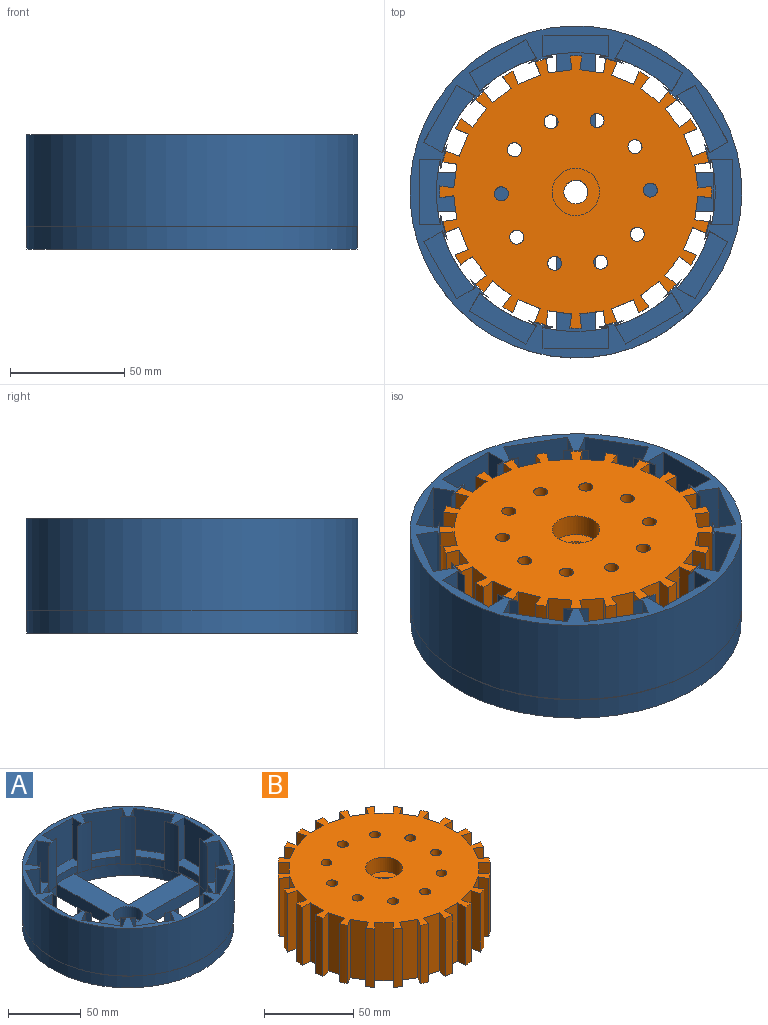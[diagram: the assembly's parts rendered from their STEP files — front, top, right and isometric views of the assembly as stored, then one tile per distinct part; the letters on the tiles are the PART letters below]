
ASSEMBLY  parts=2 mates=1
PART A: 137 faces, bbox 145.5x145.5x50 mm
  f0: cylinder r=5.26mm len=10.52mm, axis (0,0,1), area 33mm2, adj f23,f135
  f1: plane 24.96x14.43mm, normal (0,0,1), area 1.2mm2, adj f13,f103,f105,f112
  f2: plane 24.96x14.43mm, normal (0,0,1), area 1.2mm2, adj f13,f97,f99,f114
  f3: plane 122.33x122.33mm, normal (0,0,1), area 3574mm2, adj f10,f11,f12,f13,f14,f15,f16,f17
  f4: plane 24.96x14.43mm, normal (0,0,1), area 1.2mm2, adj f14,f85,f87,f118
  f5: plane 24.96x14.43mm, normal (0,0,1), area 1.2mm2, adj f14,f79,f81,f120
  f6: plane 24.96x14.43mm, normal (0,0,1), area 1.2mm2, adj f16,f67,f69,f124
  f7: plane 24.96x14.43mm, normal (0,0,1), area 1.2mm2, adj f16,f61,f63,f126
  f8: plane 24.96x14.43mm, normal (0,0,1), area 1.2mm2, adj f11,f49,f51,f130
  f9: plane 24.96x14.43mm, normal (0,0,1), area 1.2mm2, adj f11,f43,f45,f132
  f10: plane 51.98x10mm, normal (1,0,0), area 519.8mm2, adj f3,f11,f19,f23
  f11: cylinder r=61.12mm len=51.98mm, axis (0,0,1), area 788.1mm2, adj f3,f8,f9,f10,f19,f23,f33,f34
  f12: plane 51.9x10mm, normal (0,1,0), area 519mm2, adj f3,f13,f20,f23
  f13: cylinder r=61.12mm len=51.98mm, axis (0,0,1), area 788.1mm2, adj f1,f2,f3,f12,f20,f23,f30,f31
  f14: cylinder r=61.12mm len=51.98mm, axis (0,0,1), area 788.1mm2, adj f3,f4,f5,f15,f21,f23,f27,f28
  f15: plane 51.9x10mm, normal (0,-1,0), area 519mm2, adj f3,f14,f21,f23
  f16: cylinder r=61.12mm len=51.98mm, axis (0,0,1), area 788.1mm2, adj f3,f6,f7,f17,f22,f23,f24,f25
  f17: plane 51.98x10mm, normal (1,0,0), area 519.8mm2, adj f3,f16,f22,f23
  f18: cylinder r=72.41mm len=144.82mm, axis (0,0,1), area 4549.7mm2, adj f23,f110
  f19: plane 51.9x10mm, normal (0,1,0), area 519mm2, adj f3,f10,f11,f23
  f20: plane 51.98x10mm, normal (-1,0,0), area 519.8mm2, adj f3,f12,f13,f23
  f21: plane 51.98x10mm, normal (-1,0,0), area 519.8mm2, adj f3,f14,f15,f23
  f22: plane 51.9x10mm, normal (0,-1,0), area 519mm2, adj f3,f16,f17,f23
  f23: plane 144.82x144.82mm, normal (0,0,-1), area 8533.6mm2, adj f0,f10,f11,f12,f13,f14,f15,f16
  f24: plane 10.46x3.03mm, normal (0,0,-1), area 6.2mm2, adj f16,f69,f70,f71,f72,f73
  f25: plane 7.66x7.66mm, normal (0,0,-1), area 6.2mm2, adj f16,f63,f64,f65,f66,f67
  f26: plane 10.46x3.03mm, normal (0,0,-1), area 6.2mm2, adj f16,f57,f58,f59,f60,f61
  f27: plane 10.46x3.03mm, normal (0,0,-1), area 6.2mm2, adj f14,f87,f88,f89,f90,f91
  f28: plane 7.66x7.66mm, normal (0,0,-1), area 6.2mm2, adj f14,f81,f82,f83,f84,f85
  f29: plane 10.46x3.03mm, normal (0,0,-1), area 6.2mm2, adj f14,f75,f76,f77,f78,f79
  f30: plane 10.46x3.03mm, normal (0,0,-1), area 6.2mm2, adj f13,f36,f37,f105,f106,f107
  f31: plane 7.66x7.66mm, normal (0,0,-1), area 6.2mm2, adj f13,f99,f100,f101,f102,f103
  f32: plane 10.46x3.03mm, normal (0,0,-1), area 6.2mm2, adj f13,f93,f94,f95,f96,f97
  f33: plane 10.46x3.03mm, normal (0,0,-1), area 6.2mm2, adj f11,f51,f52,f53,f54,f55
  f34: plane 7.66x7.66mm, normal (0,0,-1), area 6.2mm2, adj f11,f45,f46,f47,f48,f49
  f35: plane 10.46x3.03mm, normal (0,0,-1), area 6.2mm2, adj f11,f39,f40,f41,f42,f43
  f36: plane 40x4.14mm, normal (0,1,0), area 165.7mm2, adj f30,f37,f107,f109
  f37: plane 40x9.51mm, normal (1,0,0), area 325mm2, adj f3,f30,f36,f38,f109,f133,f134
  f38: plane 34x28.79mm, normal (0,-1,0), area 978.9mm2, adj f37,f39,f109,f133
  f39: plane 40x9.51mm, normal (-1,0,0), area 325mm2, adj f3,f35,f38,f40,f109,f133,f134
  f40: plane 40x4.14mm, normal (0,1,0), area 165.7mm2, adj f35,f39,f41,f109
  f41: cylinder r=60.06mm len=40mm, axis (0,0,-1), area 433.6mm2, adj f35,f40,f42,f109
  f42: plane 40x3.59mm, normal (0.5,0.87,0), area 165.7mm2, adj f35,f41,f43,f109
  f43: plane 40x8.24mm, normal (0.87,-0.5,0), area 325mm2, adj f9,f35,f42,f44,f109,f131,f132
  f44: plane 34x24.94mm, normal (-0.5,-0.87,0), area 978.9mm2, adj f43,f45,f109,f131
  f45: plane 40x8.24mm, normal (-0.87,0.5,0), area 325mm2, adj f9,f34,f44,f46,f109,f131,f132
  f46: plane 40x3.59mm, normal (0.5,0.87,0), area 165.7mm2, adj f34,f45,f47,f109
  f47: cylinder r=60.06mm len=40mm, axis (0,0,-1), area 433.6mm2, adj f34,f46,f48,f109
  f48: plane 40x3.59mm, normal (0.87,0.5,0), area 165.7mm2, adj f34,f47,f49,f109
  f49: plane 40x8.24mm, normal (0.5,-0.87,0), area 325mm2, adj f8,f34,f48,f50,f109,f129,f130
  f50: plane 34x24.94mm, normal (-0.87,-0.5,0), area 978.9mm2, adj f49,f51,f109,f129
  f51: plane 40x8.24mm, normal (-0.5,0.87,0), area 325mm2, adj f8,f33,f50,f52,f109,f129,f130
  f52: plane 40x3.59mm, normal (0.87,0.5,0), area 165.7mm2, adj f33,f51,f53,f109
  f53: cylinder r=60.06mm len=40mm, axis (0,0,-1), area 433.6mm2, adj f33,f52,f54,f109
  f54: plane 40x4.14mm, normal (1,0,0), area 165.7mm2, adj f33,f53,f55,f109
  f55: plane 40x9.51mm, normal (0,-1,0), area 325mm2, adj f3,f33,f54,f56,f109,f127,f128
  f56: plane 34x28.79mm, normal (-1,0,0), area 978.9mm2, adj f55,f57,f109,f127
  f57: plane 40x9.51mm, normal (0,1,0), area 325mm2, adj f3,f26,f56,f58,f109,f127,f128
  f58: plane 40x4.14mm, normal (1,0,0), area 165.7mm2, adj f26,f57,f59,f109
  f59: cylinder r=60.06mm len=40mm, axis (0,0,-1), area 433.6mm2, adj f26,f58,f60,f109
  f60: plane 40x3.59mm, normal (0.87,-0.5,0), area 165.7mm2, adj f26,f59,f61,f109
  f61: plane 40x8.24mm, normal (-0.5,-0.87,0), area 325mm2, adj f7,f26,f60,f62,f109,f125,f126
  f62: plane 34x24.94mm, normal (-0.87,0.5,0), area 978.9mm2, adj f61,f63,f109,f125
  f63: plane 40x8.24mm, normal (0.5,0.87,0), area 325mm2, adj f7,f25,f62,f64,f109,f125,f126
  f64: plane 40x3.59mm, normal (0.87,-0.5,0), area 165.7mm2, adj f25,f63,f65,f109
  f65: cylinder r=60.06mm len=40mm, axis (0,0,-1), area 433.6mm2, adj f25,f64,f66,f109
  f66: plane 40x3.59mm, normal (0.5,-0.87,0), area 165.7mm2, adj f25,f65,f67,f109
  f67: plane 40x8.24mm, normal (-0.87,-0.5,0), area 325mm2, adj f6,f25,f66,f68,f109,f123,f124
  f68: plane 34x24.94mm, normal (-0.5,0.87,0), area 978.9mm2, adj f67,f69,f109,f123
  f69: plane 40x8.24mm, normal (0.87,0.5,0), area 325mm2, adj f6,f24,f68,f70,f109,f123,f124
  f70: plane 40x3.59mm, normal (0.5,-0.87,0), area 165.7mm2, adj f24,f69,f71,f109
  f71: cylinder r=60.06mm len=40mm, axis (0,0,-1), area 433.6mm2, adj f24,f70,f72,f109
  f72: plane 40x4.14mm, normal (0,-1,0), area 165.7mm2, adj f24,f71,f73,f109
  f73: plane 40x9.51mm, normal (-1,0,0), area 325mm2, adj f3,f24,f72,f74,f109,f121,f122
  f74: plane 34x28.79mm, normal (0,1,0), area 978.9mm2, adj f73,f75,f109,f121
  f75: plane 40x9.51mm, normal (1,0,0), area 325mm2, adj f3,f29,f74,f76,f109,f121,f122
  f76: plane 40x4.14mm, normal (0,-1,0), area 165.7mm2, adj f29,f75,f77,f109
  f77: cylinder r=60.06mm len=40mm, axis (0,0,-1), area 433.6mm2, adj f29,f76,f78,f109
  f78: plane 40x3.59mm, normal (-0.5,-0.87,0), area 165.7mm2, adj f29,f77,f79,f109
  f79: plane 40x8.24mm, normal (-0.87,0.5,0), area 325mm2, adj f5,f29,f78,f80,f109,f119,f120
  f80: plane 34x24.94mm, normal (0.5,0.87,0), area 978.9mm2, adj f79,f81,f109,f119
  f81: plane 40x8.24mm, normal (0.87,-0.5,0), area 325mm2, adj f5,f28,f80,f82,f109,f119,f120
  f82: plane 40x3.59mm, normal (-0.5,-0.87,0), area 165.7mm2, adj f28,f81,f83,f109
  f83: cylinder r=60.06mm len=40mm, axis (0,0,-1), area 433.6mm2, adj f28,f82,f84,f109
  f84: plane 40x3.59mm, normal (-0.87,-0.5,0), area 165.7mm2, adj f28,f83,f85,f109
  f85: plane 40x8.24mm, normal (-0.5,0.87,0), area 325mm2, adj f4,f28,f84,f86,f109,f117,f118
  f86: plane 34x24.94mm, normal (0.87,0.5,0), area 978.9mm2, adj f85,f87,f109,f117
  f87: plane 40x8.24mm, normal (0.5,-0.87,0), area 325mm2, adj f4,f27,f86,f88,f109,f117,f118
  f88: plane 40x3.59mm, normal (-0.87,-0.5,0), area 165.7mm2, adj f27,f87,f89,f109
  f89: cylinder r=60.06mm len=40mm, axis (0,0,-1), area 433.6mm2, adj f27,f88,f90,f109
  f90: plane 40x4.14mm, normal (-1,0,0), area 165.7mm2, adj f27,f89,f91,f109
  f91: plane 40x9.51mm, normal (0,1,0), area 325mm2, adj f3,f27,f90,f92,f109,f115,f116
  f92: plane 34x28.79mm, normal (1,0,0), area 978.9mm2, adj f91,f93,f109,f115
  f93: plane 40x9.51mm, normal (0,-1,0), area 325mm2, adj f3,f32,f92,f94,f109,f115,f116
  f94: plane 40x4.14mm, normal (-1,0,0), area 165.7mm2, adj f32,f93,f95,f109
  f95: cylinder r=60.06mm len=40mm, axis (0,0,-1), area 433.6mm2, adj f32,f94,f96,f109
  f96: plane 40x3.59mm, normal (-0.87,0.5,0), area 165.7mm2, adj f32,f95,f97,f109
  f97: plane 40x8.24mm, normal (0.5,0.87,0), area 325mm2, adj f2,f32,f96,f98,f109,f113,f114
  f98: plane 34x24.94mm, normal (0.87,-0.5,0), area 978.9mm2, adj f97,f99,f109,f113
  f99: plane 40x8.24mm, normal (-0.5,-0.87,0), area 325mm2, adj f2,f31,f98,f100,f109,f113,f114
  f100: plane 40x3.59mm, normal (-0.87,0.5,0), area 165.7mm2, adj f31,f99,f101,f109
  f101: cylinder r=60.06mm len=40mm, axis (0,0,-1), area 433.6mm2, adj f31,f100,f102,f109
  f102: plane 40x3.59mm, normal (-0.5,0.87,0), area 165.7mm2, adj f31,f101,f103,f109
  f103: plane 40x8.24mm, normal (0.87,0.5,0), area 325mm2, adj f1,f31,f102,f104,f109,f111,f112
  f104: plane 34x24.94mm, normal (0.5,-0.87,0), area 978.9mm2, adj f103,f105,f109,f111
  f105: plane 40x8.24mm, normal (-0.87,-0.5,0), area 325mm2, adj f1,f30,f104,f106,f109,f111,f112
  f106: plane 40x3.59mm, normal (-0.5,0.87,0), area 165.7mm2, adj f30,f105,f107,f109
  f107: cylinder r=60.06mm len=40mm, axis (0,0,-1), area 433.6mm2, adj f30,f36,f106,f109
  f108: cylinder r=72.76mm len=145.53mm, axis (0,0,-1), area 18287.3mm2, adj f109,f110
  f109: plane 145.53x145.53mm, normal (0,0,1), area 2158.4mm2, adj f36,f37,f38,f39,f40,f41,f42,f43
  f110: plane 145.53x145.53mm, normal (0,0,-1), area 160.2mm2, adj f18,f108
  f111: plane 29.56x22.4mm, normal (0,0,1), area 233mm2, adj f103,f104,f105,f112
  f112: cylinder r=61.17mm len=24.94mm, axis (0,0,-1), area 174.4mm2, adj f1,f103,f105,f111
  f113: plane 29.56x22.4mm, normal (0,0,1), area 233mm2, adj f97,f98,f99,f114
  f114: cylinder r=61.17mm len=24.94mm, axis (0,0,-1), area 174.4mm2, adj f2,f97,f99,f113
  f115: plane 28.79x9.24mm, normal (0,0,1), area 233mm2, adj f91,f92,f93,f116
  f116: cylinder r=61.17mm len=28.79mm, axis (0,0,-1), area 174.4mm2, adj f3,f91,f93,f115
  f117: plane 29.56x22.4mm, normal (0,0,1), area 233mm2, adj f85,f86,f87,f118
  f118: cylinder r=61.17mm len=24.94mm, axis (0,0,-1), area 174.4mm2, adj f4,f85,f87,f117
  f119: plane 29.56x22.4mm, normal (0,0,1), area 233mm2, adj f79,f80,f81,f120
  f120: cylinder r=61.17mm len=24.94mm, axis (0,0,-1), area 174.4mm2, adj f5,f79,f81,f119
  f121: plane 28.79x9.24mm, normal (0,0,1), area 233mm2, adj f73,f74,f75,f122
  f122: cylinder r=61.17mm len=28.79mm, axis (0,0,-1), area 174.4mm2, adj f3,f73,f75,f121
  f123: plane 29.56x22.4mm, normal (0,0,1), area 233mm2, adj f67,f68,f69,f124
  f124: cylinder r=61.17mm len=24.94mm, axis (0,0,-1), area 174.4mm2, adj f6,f67,f69,f123
  f125: plane 29.56x22.4mm, normal (0,0,1), area 233mm2, adj f61,f62,f63,f126
  f126: cylinder r=61.17mm len=24.94mm, axis (0,0,-1), area 174.4mm2, adj f7,f61,f63,f125
  f127: plane 28.79x9.24mm, normal (0,0,1), area 233mm2, adj f55,f56,f57,f128
  f128: cylinder r=61.17mm len=28.79mm, axis (0,0,-1), area 174.4mm2, adj f3,f55,f57,f127
  f129: plane 29.56x22.4mm, normal (0,0,1), area 233mm2, adj f49,f50,f51,f130
  f130: cylinder r=61.17mm len=24.94mm, axis (0,0,-1), area 174.4mm2, adj f8,f49,f51,f129
  f131: plane 29.56x22.4mm, normal (0,0,1), area 233mm2, adj f43,f44,f45,f132
  f132: cylinder r=61.17mm len=24.94mm, axis (0,0,-1), area 174.4mm2, adj f9,f43,f45,f131
  f133: plane 28.79x9.24mm, normal (0,0,1), area 233mm2, adj f37,f38,f39,f134
  f134: cylinder r=61.17mm len=28.79mm, axis (0,0,-1), area 174.4mm2, adj f3,f37,f39,f133
  f135: plane 20.08x20.08mm, normal (0,0,1), area 229.7mm2, adj f0,f136
  f136: cylinder r=10.04mm len=20.08mm, axis (0,0,1), area 567.6mm2, adj f3,f135
PART B: 111 faces, bbox 118.9x118.9x40 mm
  f0: cylinder r=5.24mm len=30mm, axis (0,0,-1), area 987.7mm2, adj f98,f100
  f1: plane 40x6.18mm, normal (1,0,0), area 247mm2, adj f2,f96,f97,f98
  f2: cylinder r=59.69mm len=40mm, axis (0,0,-1), area 205.3mm2, adj f1,f3,f97,f98
  f3: plane 40x5.97mm, normal (-0.97,-0.26,0), area 247mm2, adj f2,f4,f97,f98
  f4: plane 40x10.12mm, normal (-0.26,0.97,0), area 419.2mm2, adj f3,f5,f97,f98
  f5: plane 40x5.97mm, normal (0.97,0.26,0), area 247mm2, adj f4,f6,f97,f98
  f6: cylinder r=59.69mm len=40mm, axis (0,0,-1), area 205.3mm2, adj f5,f7,f97,f98
  f7: plane 40x5.35mm, normal (-0.87,-0.5,0), area 247mm2, adj f6,f8,f97,f98
  f8: plane 40x9.08mm, normal (-0.5,0.87,0), area 419.2mm2, adj f7,f9,f97,f98
  f9: plane 40x5.35mm, normal (0.87,0.5,0), area 247mm2, adj f8,f10,f97,f98
  f10: cylinder r=59.69mm len=40mm, axis (0,0,-1), area 205.3mm2, adj f9,f11,f97,f98
  f11: plane 40x4.37mm, normal (-0.71,-0.71,0), area 247mm2, adj f10,f12,f97,f98
  f12: plane 40x7.41mm, normal (-0.71,0.71,0), area 419.2mm2, adj f11,f13,f97,f98
  f13: plane 40x4.37mm, normal (0.71,0.71,0), area 247mm2, adj f12,f14,f97,f98
  f14: cylinder r=59.69mm len=40mm, axis (0,0,-1), area 205.3mm2, adj f13,f15,f97,f98
  f15: plane 40x5.35mm, normal (-0.5,-0.87,0), area 247mm2, adj f14,f16,f97,f98
  f16: plane 40x9.08mm, normal (-0.87,0.5,0), area 419.2mm2, adj f15,f17,f97,f98
  f17: plane 40x5.35mm, normal (0.5,0.87,0), area 247mm2, adj f16,f18,f97,f98
  f18: cylinder r=59.69mm len=40mm, axis (0,0,-1), area 205.3mm2, adj f17,f19,f97,f98
  f19: plane 40x5.97mm, normal (-0.26,-0.97,0), area 247mm2, adj f18,f20,f97,f98
  f20: plane 40x10.12mm, normal (-0.97,0.26,0), area 419.2mm2, adj f19,f21,f97,f98
  f21: plane 40x5.97mm, normal (0.26,0.97,0), area 247mm2, adj f20,f22,f97,f98
  f22: cylinder r=59.69mm len=40mm, axis (0,0,-1), area 205.3mm2, adj f21,f23,f97,f98
  f23: plane 40x6.18mm, normal (0,-1,0), area 247mm2, adj f22,f24,f97,f98
  f24: plane 40x10.48mm, normal (-1,0,0), area 419.2mm2, adj f23,f25,f97,f98
  f25: plane 40x6.18mm, normal (0,1,0), area 247mm2, adj f24,f26,f97,f98
  f26: cylinder r=59.69mm len=40mm, axis (0,0,-1), area 205.3mm2, adj f25,f27,f97,f98
  f27: plane 40x5.97mm, normal (0.26,-0.97,0), area 247mm2, adj f26,f28,f97,f98
  f28: plane 40x10.12mm, normal (-0.97,-0.26,0), area 419.2mm2, adj f27,f29,f97,f98
  f29: plane 40x5.97mm, normal (-0.26,0.97,0), area 247mm2, adj f28,f30,f97,f98
  f30: cylinder r=59.69mm len=40mm, axis (0,0,-1), area 205.3mm2, adj f29,f31,f97,f98
  f31: plane 40x5.35mm, normal (0.5,-0.87,0), area 247mm2, adj f30,f32,f97,f98
  f32: plane 40x9.08mm, normal (-0.87,-0.5,0), area 419.2mm2, adj f31,f33,f97,f98
  f33: plane 40x5.35mm, normal (-0.5,0.87,0), area 247mm2, adj f32,f34,f97,f98
  f34: cylinder r=59.69mm len=40mm, axis (0,0,-1), area 205.3mm2, adj f33,f35,f97,f98
  f35: plane 40x4.37mm, normal (0.71,-0.71,0), area 247mm2, adj f34,f36,f97,f98
  f36: plane 40x7.41mm, normal (-0.71,-0.71,0), area 419.2mm2, adj f35,f37,f97,f98
  f37: plane 40x4.37mm, normal (-0.71,0.71,0), area 247mm2, adj f36,f38,f97,f98
  f38: cylinder r=59.69mm len=40mm, axis (0,0,-1), area 205.3mm2, adj f37,f39,f97,f98
  f39: plane 40x5.35mm, normal (0.87,-0.5,0), area 247mm2, adj f38,f40,f97,f98
  f40: plane 40x9.08mm, normal (-0.5,-0.87,0), area 419.2mm2, adj f39,f41,f97,f98
  f41: plane 40x5.35mm, normal (-0.87,0.5,0), area 247mm2, adj f40,f42,f97,f98
  f42: cylinder r=59.69mm len=40mm, axis (0,0,-1), area 205.3mm2, adj f41,f43,f97,f98
  f43: plane 40x5.97mm, normal (0.97,-0.26,0), area 247mm2, adj f42,f44,f97,f98
  f44: plane 40x10.12mm, normal (-0.26,-0.97,0), area 419.2mm2, adj f43,f45,f97,f98
  f45: plane 40x5.97mm, normal (-0.97,0.26,0), area 247mm2, adj f44,f46,f97,f98
  f46: cylinder r=59.69mm len=40mm, axis (0,0,-1), area 205.3mm2, adj f45,f47,f97,f98
  f47: plane 40x6.18mm, normal (1,0,0), area 247mm2, adj f46,f48,f97,f98
  f48: plane 40x10.48mm, normal (0,-1,0), area 419.2mm2, adj f47,f49,f97,f98
  f49: plane 40x6.18mm, normal (-1,0,0), area 247mm2, adj f48,f50,f97,f98
  f50: cylinder r=59.69mm len=40mm, axis (0,0,-1), area 205.3mm2, adj f49,f51,f97,f98
  f51: plane 40x5.97mm, normal (0.97,0.26,0), area 247mm2, adj f50,f52,f97,f98
  f52: plane 40x10.12mm, normal (0.26,-0.97,0), area 419.2mm2, adj f51,f53,f97,f98
  f53: plane 40x5.97mm, normal (-0.97,-0.26,0), area 247mm2, adj f52,f54,f97,f98
  f54: cylinder r=59.69mm len=40mm, axis (0,0,-1), area 205.3mm2, adj f53,f55,f97,f98
  f55: plane 40x5.35mm, normal (0.87,0.5,0), area 247mm2, adj f54,f56,f97,f98
  f56: plane 40x9.08mm, normal (0.5,-0.87,0), area 419.2mm2, adj f55,f57,f97,f98
  f57: plane 40x5.35mm, normal (-0.87,-0.5,0), area 247mm2, adj f56,f58,f97,f98
  f58: cylinder r=59.69mm len=40mm, axis (0,0,-1), area 205.3mm2, adj f57,f59,f97,f98
  f59: plane 40x4.37mm, normal (0.71,0.71,0), area 247mm2, adj f58,f60,f97,f98
  f60: plane 40x7.41mm, normal (0.71,-0.71,0), area 419.2mm2, adj f59,f61,f97,f98
  f61: plane 40x4.37mm, normal (-0.71,-0.71,0), area 247mm2, adj f60,f62,f97,f98
  f62: cylinder r=59.69mm len=40mm, axis (0,0,-1), area 205.3mm2, adj f61,f63,f97,f98
  f63: plane 40x5.35mm, normal (0.5,0.87,0), area 247mm2, adj f62,f64,f97,f98
  f64: plane 40x9.08mm, normal (0.87,-0.5,0), area 419.2mm2, adj f63,f65,f97,f98
  f65: plane 40x5.35mm, normal (-0.5,-0.87,0), area 247mm2, adj f64,f66,f97,f98
  f66: cylinder r=59.69mm len=40mm, axis (0,0,-1), area 205.3mm2, adj f65,f67,f97,f98
  f67: plane 40x5.97mm, normal (0.26,0.97,0), area 247mm2, adj f66,f68,f97,f98
  f68: plane 40x10.12mm, normal (0.97,-0.26,0), area 419.2mm2, adj f67,f69,f97,f98
  f69: plane 40x5.97mm, normal (-0.26,-0.97,0), area 247mm2, adj f68,f70,f97,f98
  f70: cylinder r=59.69mm len=40mm, axis (0,0,-1), area 205.3mm2, adj f69,f71,f97,f98
  f71: plane 40x6.18mm, normal (0,1,0), area 247mm2, adj f70,f72,f97,f98
  f72: plane 40x10.48mm, normal (1,0,0), area 419.2mm2, adj f71,f73,f97,f98
  f73: plane 40x6.18mm, normal (0,-1,0), area 247mm2, adj f72,f74,f97,f98
  f74: cylinder r=59.69mm len=40mm, axis (0,0,-1), area 205.3mm2, adj f73,f75,f97,f98
  f75: plane 40x5.97mm, normal (-0.26,0.97,0), area 247mm2, adj f74,f76,f97,f98
  f76: plane 40x10.12mm, normal (0.97,0.26,0), area 419.2mm2, adj f75,f77,f97,f98
  f77: plane 40x5.97mm, normal (0.26,-0.97,0), area 247mm2, adj f76,f78,f97,f98
  f78: cylinder r=59.69mm len=40mm, axis (0,0,-1), area 205.3mm2, adj f77,f79,f97,f98
  f79: plane 40x5.35mm, normal (-0.5,0.87,0), area 247mm2, adj f78,f80,f97,f98
  f80: plane 40x9.08mm, normal (0.87,0.5,0), area 419.2mm2, adj f79,f81,f97,f98
  f81: plane 40x5.35mm, normal (0.5,-0.87,0), area 247mm2, adj f80,f82,f97,f98
  f82: cylinder r=59.69mm len=40mm, axis (0,0,-1), area 205.3mm2, adj f81,f83,f97,f98
  f83: plane 40x4.37mm, normal (-0.71,0.71,0), area 247mm2, adj f82,f84,f97,f98
  f84: plane 40x7.41mm, normal (0.71,0.71,0), area 419.2mm2, adj f83,f85,f97,f98
  f85: plane 40x4.37mm, normal (0.71,-0.71,0), area 247mm2, adj f84,f86,f97,f98
  f86: cylinder r=59.69mm len=40mm, axis (0,0,-1), area 205.3mm2, adj f85,f87,f97,f98
  f87: plane 40x5.35mm, normal (-0.87,0.5,0), area 247mm2, adj f86,f88,f97,f98
  f88: plane 40x9.08mm, normal (0.5,0.87,0), area 419.2mm2, adj f87,f89,f97,f98
  f89: plane 40x5.35mm, normal (0.87,-0.5,0), area 247mm2, adj f88,f90,f97,f98
  f90: cylinder r=59.69mm len=40mm, axis (0,0,-1), area 205.3mm2, adj f89,f91,f97,f98
  f91: plane 40x5.97mm, normal (-0.97,0.26,0), area 247mm2, adj f90,f92,f97,f98
  f92: plane 40x10.12mm, normal (0.26,0.97,0), area 419.2mm2, adj f91,f93,f97,f98
  f93: plane 40x5.97mm, normal (0.97,-0.26,0), area 247mm2, adj f92,f94,f97,f98
  f94: cylinder r=59.69mm len=40mm, axis (0,0,-1), area 205.3mm2, adj f93,f95,f97,f98
  f95: plane 40x6.18mm, normal (-1,0,0), area 247mm2, adj f94,f96,f97,f98
  f96: plane 40x10.48mm, normal (0,1,0), area 419.2mm2, adj f1,f95,f97,f98
  f97: plane 118.91x118.91mm, normal (0,0,1), area 8965.3mm2, adj f1,f2,f3,f4,f5,f6,f7,f8
  f98: plane 118.91x118.91mm, normal (0,0,-1), area 9217mm2, adj f0,f1,f2,f3,f4,f5,f6,f7
  f99: cylinder r=10.37mm len=20.74mm, axis (0,0,-1), area 651.6mm2, adj f97,f100
  f100: plane 20.74x20.74mm, normal (0,0,1), area 251.6mm2, adj f0,f99
  f101: cylinder r=3.07mm len=40mm, axis (0,0,-1), area 772.4mm2, adj f97,f98
  f102: cylinder r=3.07mm len=40mm, axis (0,0,-1), area 772.4mm2, adj f97,f98
  f103: cylinder r=3.07mm len=40mm, axis (0,0,-1), area 772.4mm2, adj f97,f98
  f104: cylinder r=3.07mm len=40mm, axis (0,0,-1), area 772.4mm2, adj f97,f98
  f105: cylinder r=3.07mm len=40mm, axis (0,0,-1), area 772.4mm2, adj f97,f98
  f106: cylinder r=3.07mm len=40mm, axis (0,0,-1), area 772.4mm2, adj f97,f98
  f107: cylinder r=3.07mm len=40mm, axis (0,0,-1), area 772.4mm2, adj f97,f98
  f108: cylinder r=3.07mm len=40mm, axis (0,0,-1), area 772.4mm2, adj f97,f98
  f109: cylinder r=3.07mm len=40mm, axis (0,0,-1), area 772.4mm2, adj f97,f98
  f110: cylinder r=3.07mm len=40mm, axis (0,0,-1), area 772.4mm2, adj f97,f98
PLACE A t=(2.54,-10.64,-9.69)mm fixed
PLACE B rot(axis=(0,0,-1),52.6deg) t=(2.54,-10.64,-9.69)mm
MATE revolute B.f0 <-> A.f13  axis (0,0,-1) through (2.54,-10.64,-9.69)mm
